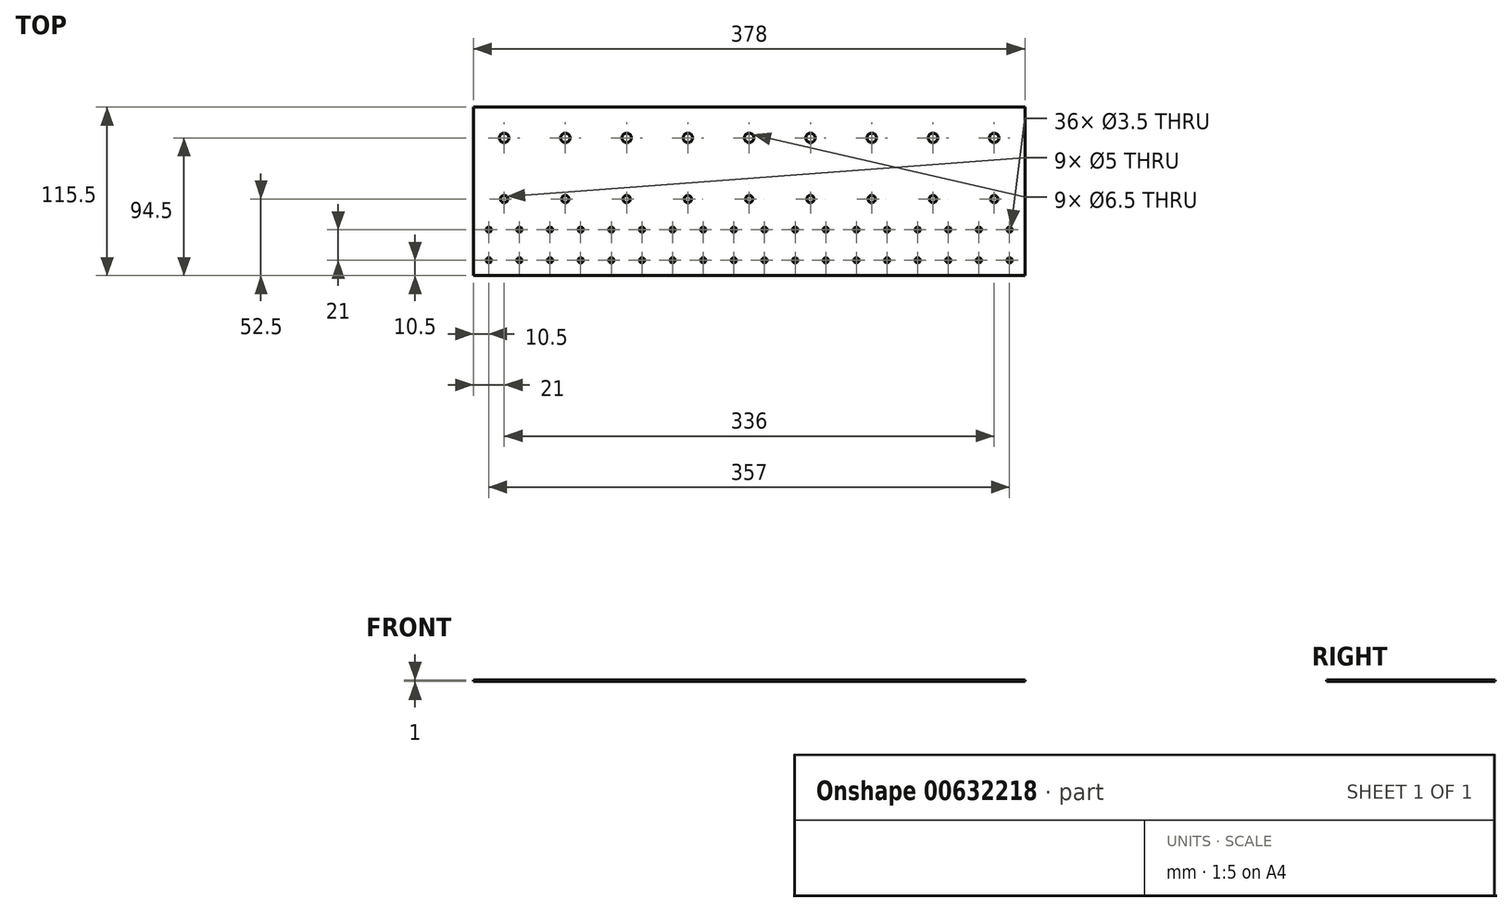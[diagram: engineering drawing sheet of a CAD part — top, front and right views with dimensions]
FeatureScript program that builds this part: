
annotation { "Feature Type Name" : "Feature", "Feature Type Description" : "" }
export const myFeature = defineFeature(function(context is Context, id is Id, definition is map)
    precondition{}
    {
        {
            var Q0;
            Q0=qCreatedBy(makeId("Top.planeOp"),FACE);
            var sketch = newSketch(context, id + "F0", { "sketchPlane" : qUnion([Q0])});
            skLineSegment(sketch, "E0.bottom", {"start": v(0, 0) * mm, "end": v(378, 0) * mm});
            skLineSegment(sketch, "E0.top", {"start": v(0, 115.5) * mm, "end": v(378, 115.5) * mm});
            skLineSegment(sketch, "E0.left", {"start": v(0, 0) * mm, "end": v(0, 115.5) * mm});
            skLineSegment(sketch, "E0.right", {"start": v(378, 0) * mm, "end": v(378, 115.5) * mm});
            skCircle(sketch, "E1", {"center": v(21, 94.5) * mm, "radius": 3.25 * mm});
            skCircle(sketch, "E2.1.0.0", {"center": v(63, 94.5) * mm, "radius": 3.25 * mm});
            skCircle(sketch, "E2.2.0.0", {"center": v(105, 94.5) * mm, "radius": 3.25 * mm});
            skCircle(sketch, "E2.3.0.0", {"center": v(147, 94.5) * mm, "radius": 3.25 * mm});
            skCircle(sketch, "E2.4.0.0", {"center": v(189, 94.5) * mm, "radius": 3.25 * mm});
            skCircle(sketch, "E2.5.0.0", {"center": v(231, 94.5) * mm, "radius": 3.25 * mm});
            skCircle(sketch, "E2.6.0.0", {"center": v(273, 94.5) * mm, "radius": 3.25 * mm});
            skCircle(sketch, "E2.7.0.0", {"center": v(315, 94.5) * mm, "radius": 3.25 * mm});
            skCircle(sketch, "E2.8.0.0", {"center": v(357, 94.5) * mm, "radius": 3.25 * mm});
            skLineSegment(sketch, "E2.direction1", {"start": v(21, 94.5) * mm, "end": v(63, 94.5) * mm, "construction": true});
            skCircle(sketch, "E3", {"center": v(21, 52.5) * mm, "radius": 2.5 * mm});
            skCircle(sketch, "E4", {"center": v(10.5, 31.5) * mm, "radius": 1.75 * mm});
            skCircle(sketch, "E5.1.0.0", {"center": v(63, 52.5) * mm, "radius": 2.5 * mm});
            skCircle(sketch, "E5.2.0.0", {"center": v(105, 52.5) * mm, "radius": 2.5 * mm});
            skCircle(sketch, "E5.3.0.0", {"center": v(147, 52.5) * mm, "radius": 2.5 * mm});
            skCircle(sketch, "E5.4.0.0", {"center": v(189, 52.5) * mm, "radius": 2.5 * mm});
            skCircle(sketch, "E5.5.0.0", {"center": v(231, 52.5) * mm, "radius": 2.5 * mm});
            skCircle(sketch, "E5.6.0.0", {"center": v(273, 52.5) * mm, "radius": 2.5 * mm});
            skCircle(sketch, "E5.7.0.0", {"center": v(315, 52.5) * mm, "radius": 2.5 * mm});
            skCircle(sketch, "E5.8.0.0", {"center": v(357, 52.5) * mm, "radius": 2.5 * mm});
            skLineSegment(sketch, "E5.direction1", {"start": v(21, 52.5) * mm, "end": v(63, 52.5) * mm, "construction": true});
            skCircle(sketch, "E6.1.0.0", {"center": v(31.5, 31.5) * mm, "radius": 1.75 * mm});
            skCircle(sketch, "E6.2.0.0", {"center": v(52.5, 31.5) * mm, "radius": 1.75 * mm});
            skCircle(sketch, "E6.3.0.0", {"center": v(73.5, 31.5) * mm, "radius": 1.75 * mm});
            skCircle(sketch, "E6.4.0.0", {"center": v(94.5, 31.5) * mm, "radius": 1.75 * mm});
            skCircle(sketch, "E6.5.0.0", {"center": v(115.5, 31.5) * mm, "radius": 1.75 * mm});
            skCircle(sketch, "E6.6.0.0", {"center": v(136.5, 31.5) * mm, "radius": 1.75 * mm});
            skCircle(sketch, "E6.7.0.0", {"center": v(157.5, 31.5) * mm, "radius": 1.75 * mm});
            skCircle(sketch, "E6.8.0.0", {"center": v(178.5, 31.5) * mm, "radius": 1.75 * mm});
            skLineSegment(sketch, "E6.direction1", {"start": v(10.5, 31.5) * mm, "end": v(31.5, 31.5) * mm, "construction": true});
            skCircle(sketch, "E7.0.9.0", {"center": v(199.5, 31.5) * mm, "radius": 1.75 * mm});
            skCircle(sketch, "E7.0.10.0", {"center": v(220.5, 31.5) * mm, "radius": 1.75 * mm});
            skCircle(sketch, "E7.0.11.0", {"center": v(241.5, 31.5) * mm, "radius": 1.75 * mm});
            skCircle(sketch, "E7.0.12.0", {"center": v(262.5, 31.5) * mm, "radius": 1.75 * mm});
            skCircle(sketch, "E7.0.13.0", {"center": v(283.5, 31.5) * mm, "radius": 1.75 * mm});
            skCircle(sketch, "E7.0.14.0", {"center": v(304.5, 31.5) * mm, "radius": 1.75 * mm});
            skCircle(sketch, "E7.0.15.0", {"center": v(325.5, 31.5) * mm, "radius": 1.75 * mm});
            skCircle(sketch, "E8.0.16.0", {"center": v(346.5, 31.5) * mm, "radius": 1.75 * mm});
            skCircle(sketch, "E9", {"center": v(10.5, 10.5) * mm, "radius": 1.75 * mm});
            skCircle(sketch, "E10.1.0.0", {"center": v(31.5, 10.5) * mm, "radius": 1.75 * mm});
            skCircle(sketch, "E10.2.0.0", {"center": v(52.5, 10.5) * mm, "radius": 1.75 * mm});
            skCircle(sketch, "E10.3.0.0", {"center": v(73.5, 10.5) * mm, "radius": 1.75 * mm});
            skCircle(sketch, "E10.4.0.0", {"center": v(94.5, 10.5) * mm, "radius": 1.75 * mm});
            skCircle(sketch, "E10.5.0.0", {"center": v(115.5, 10.5) * mm, "radius": 1.75 * mm});
            skCircle(sketch, "E10.6.0.0", {"center": v(136.5, 10.5) * mm, "radius": 1.75 * mm});
            skCircle(sketch, "E10.7.0.0", {"center": v(157.5, 10.5) * mm, "radius": 1.75 * mm});
            skCircle(sketch, "E10.8.0.0", {"center": v(178.5, 10.5) * mm, "radius": 1.75 * mm});
            skCircle(sketch, "E10.9.0.0", {"center": v(199.5, 10.5) * mm, "radius": 1.75 * mm});
            skCircle(sketch, "E10.10.0.0", {"center": v(220.5, 10.5) * mm, "radius": 1.75 * mm});
            skCircle(sketch, "E10.11.0.0", {"center": v(241.5, 10.5) * mm, "radius": 1.75 * mm});
            skCircle(sketch, "E10.12.0.0", {"center": v(262.5, 10.5) * mm, "radius": 1.75 * mm});
            skCircle(sketch, "E10.13.0.0", {"center": v(283.5, 10.5) * mm, "radius": 1.75 * mm});
            skCircle(sketch, "E10.14.0.0", {"center": v(304.5, 10.5) * mm, "radius": 1.75 * mm});
            skCircle(sketch, "E10.15.0.0", {"center": v(325.5, 10.5) * mm, "radius": 1.75 * mm});
            skCircle(sketch, "E10.16.0.0", {"center": v(346.5, 10.5) * mm, "radius": 1.75 * mm});
            skLineSegment(sketch, "E10.direction1", {"start": v(10.5, 10.5) * mm, "end": v(31.5, 10.5) * mm, "construction": true});
            skCircle(sketch, "E11.0.17.0", {"center": v(367.5, 10.5) * mm, "radius": 1.75 * mm});
            skCircle(sketch, "E12.0.17.0", {"center": v(367.5, 31.5) * mm, "radius": 1.75 * mm});
            skSolve(sketch);
        }
        {
            var Q0;
            Q0=makeQuery(id+"F0.imprint","IMPRINT",FACE,{"disambiguationData":[TD([[makeQuery(id+"F0.imprint","IMPRINT",EDGE,{"derivedFrom":sQuery(id+"F0.wireOp",EDGE,"E0.bottom")}),1.0]])]});
            extrude(context, id + "F1", {"entities" : qUnion([Q0]), "depth" : 1 * mm, "offsetDistance" : 25 * mm});
        }
    });
